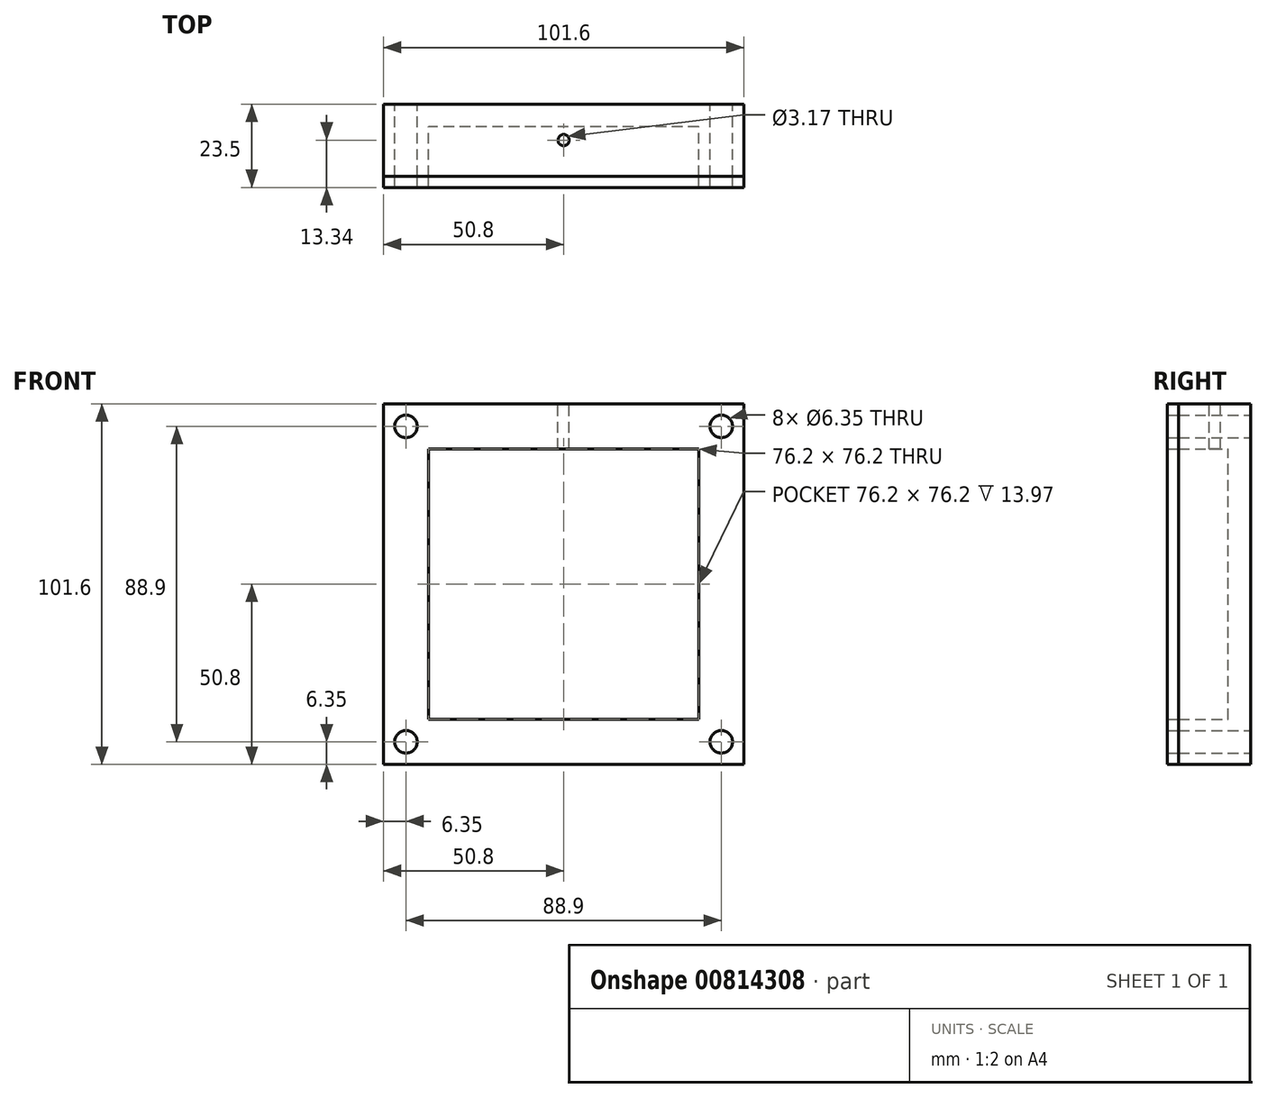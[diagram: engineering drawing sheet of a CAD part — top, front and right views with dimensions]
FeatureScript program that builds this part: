
annotation { "Feature Type Name" : "Feature", "Feature Type Description" : "" }
export const myFeature = defineFeature(function(context is Context, id is Id, definition is map)
    precondition{}
    {
        {
            var Q0;
            Q0=qCreatedBy(makeId("Front.planeOp"),FACE);
            var sketch = newSketch(context, id + "F0", { "sketchPlane" : qUnion([Q0])});
            skLineSegment(sketch, "E0", {"start": v(38.1, 0) * mm, "end": v(38.1, 38.1) * mm});
            skLineSegment(sketch, "E1.MirrorCS", {"start": v(38.1, 0) * mm, "end": v(38.1, -38.1) * mm});
            skLineSegment(sketch, "E2.MirrorCS", {"start": v(-38.1, 0) * mm, "end": v(-38.1, 38.1) * mm});
            skLineSegment(sketch, "E3.MirrorCS", {"start": v(-38.1, 0) * mm, "end": v(-38.1, -38.1) * mm});
            skLineSegment(sketch, "E4", {"start": v(-38.1, -38.1) * mm, "end": v(38.1, -38.1) * mm});
            skLineSegment(sketch, "E5", {"start": v(-38.1, 38.1) * mm, "end": v(38.1, 38.1) * mm});
            skLineSegment(sketch, "E6", {"start": v(38.1, 38.1) * mm, "end": v(50.8, 38.1) * mm});
            skLineSegment(sketch, "E7", {"start": v(50.8, 38.1) * mm, "end": v(50.8, -50.8) * mm});
            skLineSegment(sketch, "E8", {"start": v(50.8, -50.8) * mm, "end": v(-50.8, -50.8) * mm});
            skLineSegment(sketch, "E9", {"start": v(-50.8, -50.8) * mm, "end": v(-50.8, 50.8) * mm});
            skLineSegment(sketch, "E10", {"start": v(-50.8, 50.8) * mm, "end": v(50.8, 50.8) * mm});
            skLineSegment(sketch, "E11", {"start": v(50.8, 50.8) * mm, "end": v(50.8, 38.1) * mm});
            skLineSegment(sketch, "E12", {"start": v(-38.1, 38.1) * mm, "end": v(-38.1, 50.8) * mm});
            skLineSegment(sketch, "E13", {"start": v(-38.1, 50.8) * mm, "end": v(38.1, 50.8) * mm});
            skLineSegment(sketch, "E14", {"start": v(38.1, 50.8) * mm, "end": v(38.1, 38.1) * mm});
            skLineSegment(sketch, "E15", {"start": v(-50.8, 38.1) * mm, "end": v(-38.1, 38.1) * mm});
            skLineSegment(sketch, "E16", {"start": v(-38.1, 0) * mm, "end": v(-28.53, 0) * mm});
            skLineSegment(sketch, "E17", {"start": v(0, 38.1) * mm, "end": v(0, 29.89) * mm});
            skPoint(sketch, "E18", {"position": v(-44.45, 44.45) * mm});
            skPoint(sketch, "E18.positionSnap0", {"position": v(-38.1, 44.45) * mm});
            skPoint(sketch, "E18.positionSnap1", {"position": v(-44.45, 38.1) * mm});
            skCircle(sketch, "E19", {"center": v(-44.45, 44.45) * mm, "radius": 3.18 * mm});
            skCircle(sketch, "E20.MirrorC", {"center": v(44.45, 44.45) * mm, "radius": 3.18 * mm});
            skCircle(sketch, "E21.MirrorC", {"center": v(-44.45, -44.45) * mm, "radius": 3.18 * mm});
            skCircle(sketch, "E22.MirrorC", {"center": v(44.45, -44.45) * mm, "radius": 3.18 * mm});
            skSolve(sketch);
        }
        {
            var Q0;
            Q0=makeQuery(id+"F0.imprint","IMPRINT",FACE,{"disambiguationData":[TD([[makeQuery(id+"F0.imprint","IMPRINT",EDGE,{"derivedFrom":sQuery(id+"F0.wireOp",EDGE,"E0")}),-1.0]])]});
            var Q1;
            {var subQ1=sQuery(id+"F0.wireOp",EDGE,"E0");Q1=makeQuery(id+"F0.imprint","IMPRINT",FACE,{"disambiguationData":[TD([[makeQuery(id+"F0.imprint","IMPRINT",EDGE,{"derivedFrom":subQ1}),1.0]])]});}
            var Q2;
            {var subQ0=sQuery(id+"F0.wireOp",EDGE,"E12");Q2=makeQuery(id+"F0.imprint","IMPRINT",FACE,{"disambiguationData":[TD([[makeQuery(id+"F0.imprint","IMPRINT",EDGE,{"derivedFrom":subQ0}),-1.0]])]});}
            var Q3;
            {var subQ4=sQuery(id+"F0.wireOp",EDGE,"E12");Q3=makeQuery(id+"F0.imprint","IMPRINT",FACE,{"disambiguationData":[TD([[makeQuery(id+"F0.imprint","IMPRINT",EDGE,{"derivedFrom":subQ4}),1.0]])]});}
            var Q4;
            Q4=makeQuery(id+"F0.imprint","IMPRINT",FACE,{"disambiguationData":[TD([[makeQuery(id+"F0.imprint","IMPRINT",EDGE,{"derivedFrom":sQuery(id+"F0.wireOp",EDGE,"E6")}),1.0]])]});
            extrude(context, id + "F1", {"entities" : qUnion([Q0, Q1, Q2, Q3, Q4]), "depth" : 6.35 * mm, "offsetDistance" : 25.4 * mm});
        }
        {
            var Q0;
            Q0=makeQuery(id+"F0.imprint","IMPRINT",FACE,{"disambiguationData":[TD([[makeQuery(id+"F0.imprint","IMPRINT",EDGE,{"derivedFrom":sQuery(id+"F0.wireOp",EDGE,"E0")}),-1.0]])]});
            var Q1;
            {var subQ0=sQuery(id+"F0.wireOp",EDGE,"E12");Q1=makeQuery(id+"F0.imprint","IMPRINT",FACE,{"disambiguationData":[TD([[makeQuery(id+"F0.imprint","IMPRINT",EDGE,{"derivedFrom":subQ0}),-1.0]])]});}
            var Q2;
            Q2=makeQuery(id+"F0.imprint","IMPRINT",FACE,{"disambiguationData":[TD([[makeQuery(id+"F0.imprint","IMPRINT",EDGE,{"derivedFrom":sQuery(id+"F0.wireOp",EDGE,"E6")}),1.0]])]});
            var Q3;
            {var subQ4=sQuery(id+"F0.wireOp",EDGE,"E12");Q3=makeQuery(id+"F0.imprint","IMPRINT",FACE,{"disambiguationData":[TD([[makeQuery(id+"F0.imprint","IMPRINT",EDGE,{"derivedFrom":subQ4}),1.0]])]});}
            var Q4;
            Q4=qSketchRegion(id+"F3",true);
            extrude(context, id + "F2", {"entities" : qUnion([Q0, Q1, Q2, Q3, Q4]), "operationType" : NewBodyOperationType.ADD, "depth" : 20.32 * mm, "offsetDistance" : 25.4 * mm});
        }
        {
            var Q0;
            {var subQ0=sQuery(id+"F0.wireOp",EDGE,"E10");Q0=makeQuery(id+"F2.boolean.opBoolean","MERGE",FACE,{"derivedFrom":[makeQuery(id+"F1.opExtrude","SWEPT_FACE",FACE,{"disambiguationData":[OSD([subQ0])]}),makeQuery(id+"F2.opExtrude","SWEPT_FACE",FACE,{"disambiguationData":[OSD([subQ0])]})]});}
            var sketch = newSketch(context, id + "F3", { "sketchPlane" : qUnion([Q0])});
            skLineSegment(sketch, "E23", {"start": v(-50.8, 0) * mm, "end": v(50.8, 0) * mm});
            skLineSegment(sketch, "E24", {"start": v(50.8, 0) * mm, "end": v(50.8, -20.32) * mm});
            skLineSegment(sketch, "E25", {"start": v(50.8, -20.32) * mm, "end": v(-50.8, -20.32) * mm});
            skLineSegment(sketch, "E26", {"start": v(-50.8, -20.32) * mm, "end": v(-50.8, 0) * mm});
            skCircle(sketch, "E27", {"center": v(0, -10.16) * mm, "radius": 1.59 * mm});
            skSolve(sketch);
        }
        {
            var Q0;
            Q0=makeQuery(id+"F3.imprint","IMPRINT",FACE,{"disambiguationData":[TD([[makeQuery(id+"F3.imprint","IMPRINT",EDGE,{"derivedFrom":sQuery(id+"F3.wireOp",EDGE,"E27")}),1.0]])]});
            extrude(context, id + "F4", {"entities" : qUnion([Q0]), "operationType" : NewBodyOperationType.REMOVE, "oppositeDirection" : true, "depth" : 25.4 * mm, "offsetDistance" : 25.4 * mm});
        }
        {
            var Q0;
            Q0=makeQuery(id+"F2.opExtrude","CAP_FACE",FACE,{"disambiguationData":[OSD([sQuery(id+"F0.wireOp",EDGE,"E0"),sQuery(id+"F0.wireOp",EDGE,"E1.MirrorCS"),sQuery(id+"F0.wireOp",EDGE,"E2.MirrorCS"),sQuery(id+"F0.wireOp",EDGE,"E3.MirrorCS"),sQuery(id+"F0.wireOp",EDGE,"E4"),sQuery(id+"F0.wireOp",EDGE,"E5"),sQuery(id+"F0.wireOp",EDGE,"E7"),sQuery(id+"F0.wireOp",EDGE,"E8"),sQuery(id+"F0.wireOp",EDGE,"E9"),sQuery(id+"F0.wireOp",EDGE,"E10"),sQuery(id+"F0.wireOp",EDGE,"E11"),sQuery(id+"F0.wireOp",EDGE,"E19"),sQuery(id+"F0.wireOp",EDGE,"E20.MirrorC"),sQuery(id+"F0.wireOp",EDGE,"E21.MirrorC"),sQuery(id+"F0.wireOp",EDGE,"E22.MirrorC")])],"isStart":false});
            var sketch = newSketch(context, id + "F5", { "sketchPlane" : qUnion([Q0])});
            skLineSegment(sketch, "E28", {"start": v(-50.8, 50.8) * mm, "end": v(50.8, 50.8) * mm});
            skLineSegment(sketch, "E29", {"start": v(50.8, 50.8) * mm, "end": v(50.8, -50.8) * mm});
            skLineSegment(sketch, "E30", {"start": v(50.8, -50.8) * mm, "end": v(-50.8, -50.8) * mm});
            skLineSegment(sketch, "E31", {"start": v(-50.8, -50.8) * mm, "end": v(-50.8, 50.8) * mm});
            skLineSegment(sketch, "E32", {"start": v(-38.1, 38.1) * mm, "end": v(38.1, 38.1) * mm});
            skLineSegment(sketch, "E33", {"start": v(38.1, 38.1) * mm, "end": v(38.1, -38.1) * mm});
            skLineSegment(sketch, "E34", {"start": v(38.1, -38.1) * mm, "end": v(-38.1, -38.1) * mm});
            skLineSegment(sketch, "E35", {"start": v(-38.1, -38.1) * mm, "end": v(-38.1, 38.1) * mm});
            skSolve(sketch);
        }
        {
            var Q0;
            Q0=makeQuery(id+"F5.imprint","IMPRINT",FACE,{"disambiguationData":[TD([[makeQuery(id+"F5.imprint","IMPRINT",EDGE,{"derivedFrom":sQuery(id+"F5.wireOp",EDGE,"E28")}),-1.0]])]});
            extrude(context, id + "F6", {"entities" : qUnion([Q0]), "depth" : 3.17 * mm, "offsetDistance" : 25.4 * mm});
        }
    });
